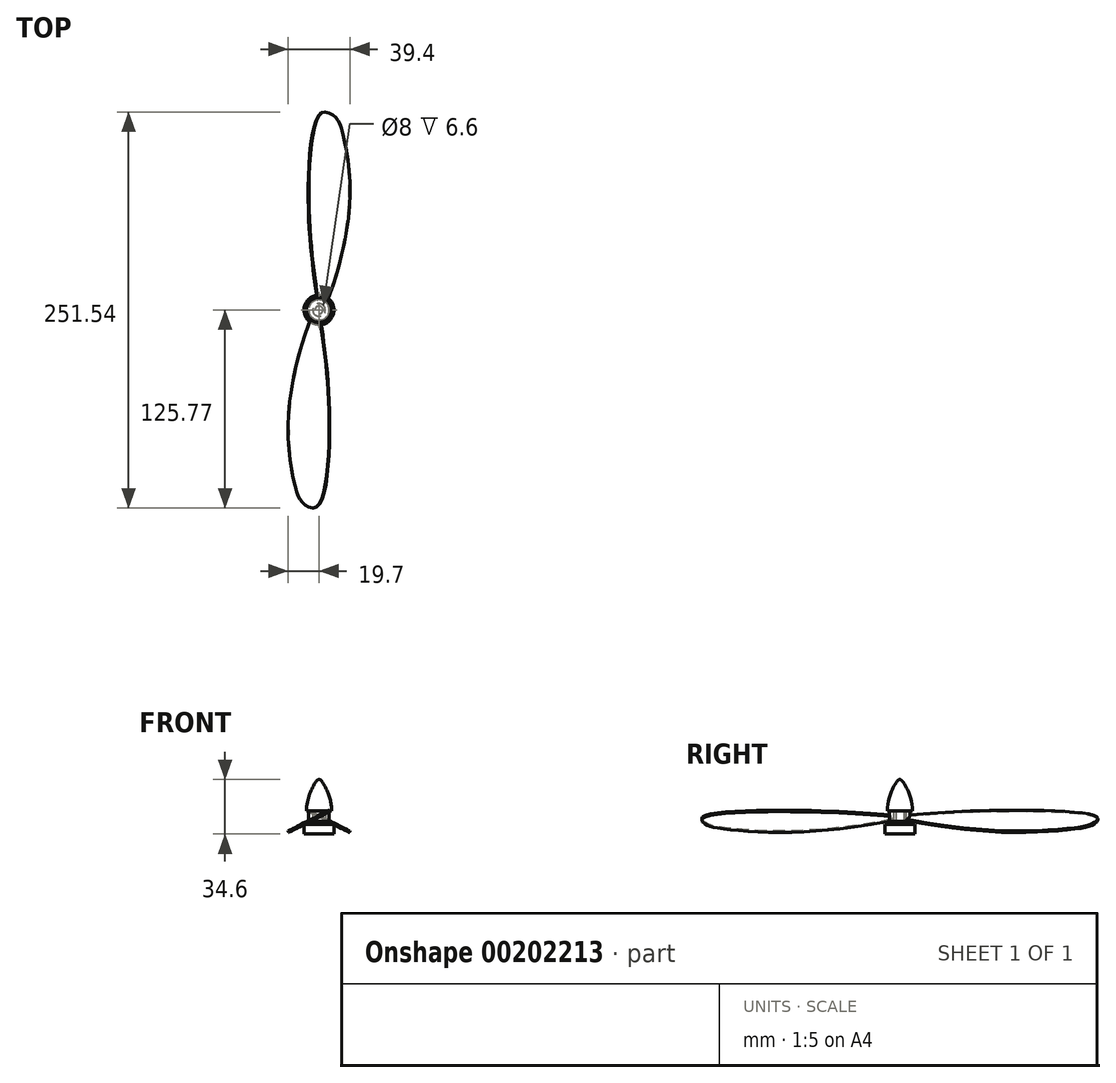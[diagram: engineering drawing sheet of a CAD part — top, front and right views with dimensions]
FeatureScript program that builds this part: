
annotation { "Feature Type Name" : "Feature", "Feature Type Description" : "" }
export const myFeature = defineFeature(function(context is Context, id is Id, definition is map)
    precondition{}
    {
        {
            var Q0;
            Q0=qCreatedBy(makeId("Top.planeOp"),FACE);
            var sketch = newSketch(context, id + "F0", { "sketchPlane" : qUnion([Q0])});
            skCircle(sketch, "E0", {"center": v(0, 0) * mm, "radius": 6.5 * mm});
            skCircle(sketch, "E1", {"center": v(0, 0) * mm, "radius": 4 * mm});
            skSolve(sketch);
        }
        {
            var Q0;
            Q0=qSketchRegion(id+"F0",true);
            extrude(context, id + "F1", {"entities" : qUnion([Q0]), "depth" : 6.6 * mm});
        }
        {
            var Q0;
            Q0=qCreatedBy(makeId("Front.planeOp"),FACE);
            var sketch = newSketch(context, id + "F2", { "sketchPlane" : qUnion([Q0])});
            skLineSegment(sketch, "E2", {"start": v(6.5, 6.6) * mm, "end": v(-6.5, 0) * mm});
            skLineSegment(sketch, "E3", {"start": v(0, 0) * mm, "end": v(0, 13.96) * mm, "construction": true});
            skSolve(sketch);
        }
        {
            var Q0;
            Q0=sQuery(id+"F2.wireOp",EDGE,"E2");
            cPlane(context, id + "F3", {"entities" : qUnion([Q0]), "cplaneType" : CPlaneType.LINE_ANGLE, "offset" : 25 * mm, "angle" : 90 * degree, "width" : 150 * mm, "height" : 150 * mm});
        }
        {
            var Q0;
            Q0=qCreatedBy(id+"F3.planeOp",FACE);
            var sketch = newSketch(context, id + "F4", { "sketchPlane" : qUnion([Q0])});
            skFitSpline(sketch, "E4", {"points": [v(0, 0) * mm, v(-4.66, -6.7) * mm, v(-20.13, -68.04) * mm, v(-14.06, -115.71) * mm, v(-9.47, -122.82) * mm, v(0, -125) * mm, v(8.87, -68.04) * mm, v(3.8, -14.65) * mm, v(0, 0) * mm]});
            skSolve(sketch);
        }
        {
            var Q0;
            Q0=qSketchRegion(id+"F4",true);
            extrude(context, id + "F5", {"entities" : qUnion([Q0]), "operationType" : NewBodyOperationType.ADD, "depth" : 0.5 * mm, "hasSecondDirection" : true, "secondDirectionOppositeDirection" : true, "secondDirectionDepth" : 0.5 * mm});
        }
        {
            var Q0;
            Q0=makeQuery(id+"F1.opExtrude","SWEPT_BODY",BODY,{"disambiguationData":[OSD([sQuery(id+"F0.wireOp",EDGE,"E0"),sQuery(id+"F0.wireOp",EDGE,"E1")])]});
            var Q1;
            Q1=sQuery(id+"F2.wireOp",EDGE,"E3");
            circularPattern(context, id + "F6", {"entities" : qUnion([Q0]), "axis" : qUnion([Q1]), "angle" : 360 * degree, "instanceCount" : 2, "equalSpace" : true});
        }
        {
            var Q0;
            Q0=makeQuery(id+"F0.imprint","IMPRINT",FACE,{"disambiguationData":[TD([[makeQuery(id+"F0.imprint","IMPRINT",EDGE,{"derivedFrom":sQuery(id+"F0.wireOp",EDGE,"E1")}),1.0]])]});
            extrude(context, id + "F7", {"entities" : qUnion([Q0]), "operationType" : NewBodyOperationType.REMOVE, "depth" : 25 * mm});
        }
        {
            var Q0;
            Q0=makeQuery(id+"F1.opExtrude","CAP_FACE",FACE,{"disambiguationData":[OSD([sQuery(id+"F0.wireOp",EDGE,"E0"),sQuery(id+"F0.wireOp",EDGE,"E1")])],"isStart":true});
            var sketch = newSketch(context, id + "F8", { "sketchPlane" : qUnion([Q0])});
            skCircle(sketch, "E5", {"center": v(0, 0) * mm, "radius": 8 * mm});
            skCircle(sketch, "E6", {"center": v(0, 0) * mm, "radius": 2.5 * mm});
            skSolve(sketch);
        }
        {
            var Q0;
            Q0=qSketchRegion(id+"F8",true);
            extrude(context, id + "F9", {"entities" : qUnion([Q0]), "depth" : 2 * mm});
        }
        {
            var Q0;
            Q0=makeQuery(id+"F9.opExtrude","CAP_FACE",FACE,{"disambiguationData":[OSD([sQuery(id+"F8.wireOp",EDGE,"E5"),sQuery(id+"F8.wireOp",EDGE,"E6")])],"isStart":false});
            var sketch = newSketch(context, id + "F10", { "sketchPlane" : qUnion([Q0])});
            skCircle(sketch, "E7", {"center": v(0, 0) * mm, "radius": 9.5 * mm});
            skCircle(sketch, "E8", {"center": v(0, 0) * mm, "radius": 2.5 * mm});
            skSolve(sketch);
        }
        {
            var Q0;
            Q0=makeQuery(id+"F10.imprint","IMPRINT",FACE,{"disambiguationData":[TD([[makeQuery(id+"F10.imprint","IMPRINT",EDGE,{"derivedFrom":sQuery(id+"F10.wireOp",EDGE,"E7")}),1.0]])]});
            var Q1;
            Q1=makeQuery(id+"F10.imprint","IMPRINT",FACE,{"disambiguationData":[TD([[makeQuery(id+"F10.imprint","IMPRINT",EDGE,{"derivedFrom":sQuery(id+"F10.wireOp",EDGE,"E8")}),-1.0]])]});
            var Q2;
            Q2=makeQuery(id+"F10.imprint","IMPRINT",FACE,{"disambiguationData":[TD([[makeQuery(id+"F10.imprint","IMPRINT",EDGE,{"derivedFrom":sQuery(id+"F10.wireOp",EDGE,"E8")}),1.0]])]});
            extrude(context, id + "F11", {"entities" : qUnion([Q0, Q1, Q2]), "operationType" : NewBodyOperationType.ADD, "depth" : 6 * mm});
        }
        {
            var Q0;
            Q0=makeQuery(id+"F11.boolean.opBoolean","SPLIT",FACE,{"disambiguationData":[TD([makeQuery(id+"F9.opExtrude","SWEPT_FACE",FACE,{"disambiguationData":[OSD([sQuery(id+"F8.wireOp",EDGE,"E6")])]})])],"derivedFrom":makeQuery(id+"F11.opExtrude","CAP_FACE",FACE,{"disambiguationData":[OSD([sQuery(id+"F10.wireOp",EDGE,"E7")])],"isStart":true})});
            extrude(context, id + "F12", {"entities" : qUnion([Q0]), "operationType" : NewBodyOperationType.ADD, "depth" : 19 * mm});
        }
        {
            var Q0;
            Q0=qCreatedBy(makeId("Front.planeOp"),FACE);
            var sketch = newSketch(context, id + "F13", { "sketchPlane" : qUnion([Q0])});
            skLineSegment(sketch, "E9", {"start": v(0, 6.6) * mm, "end": v(-8, 6.6) * mm});
            skLineSegment(sketch, "E10", {"start": v(0, 6.6) * mm, "end": v(0, 26.6) * mm});
            skFitSpline(sketch, "E11", {"points": [v(0, 26.6) * mm, v(-1.7, 25.48) * mm, v(-8, 6.6) * mm], "startDerivative": vector(-7.16, 0) * mm, "endDerivative": vector(0, -33.76) * mm});
            skLineSegment(sketch, "E12", {"start": v(0, 26.6) * mm, "end": v(-3.42, 26.6) * mm, "construction": true});
            skLineSegment(sketch, "E13", {"start": v(-8, 6.6) * mm, "end": v(-8, 11.18) * mm, "construction": true});
            skSolve(sketch);
        }
        {
            var Q0;
            Q0=qSketchRegion(id+"F13",true);
            var Q1;
            Q1=sQuery(id+"F13.wireOp",EDGE,"E10");
            revolve(context, id + "F14", {"operationType" : NewBodyOperationType.ADD, "entities" : qUnion([Q0]), "axis" : qUnion([Q1]), "revolveType" : RevolveType.FULL});
        }
    });
